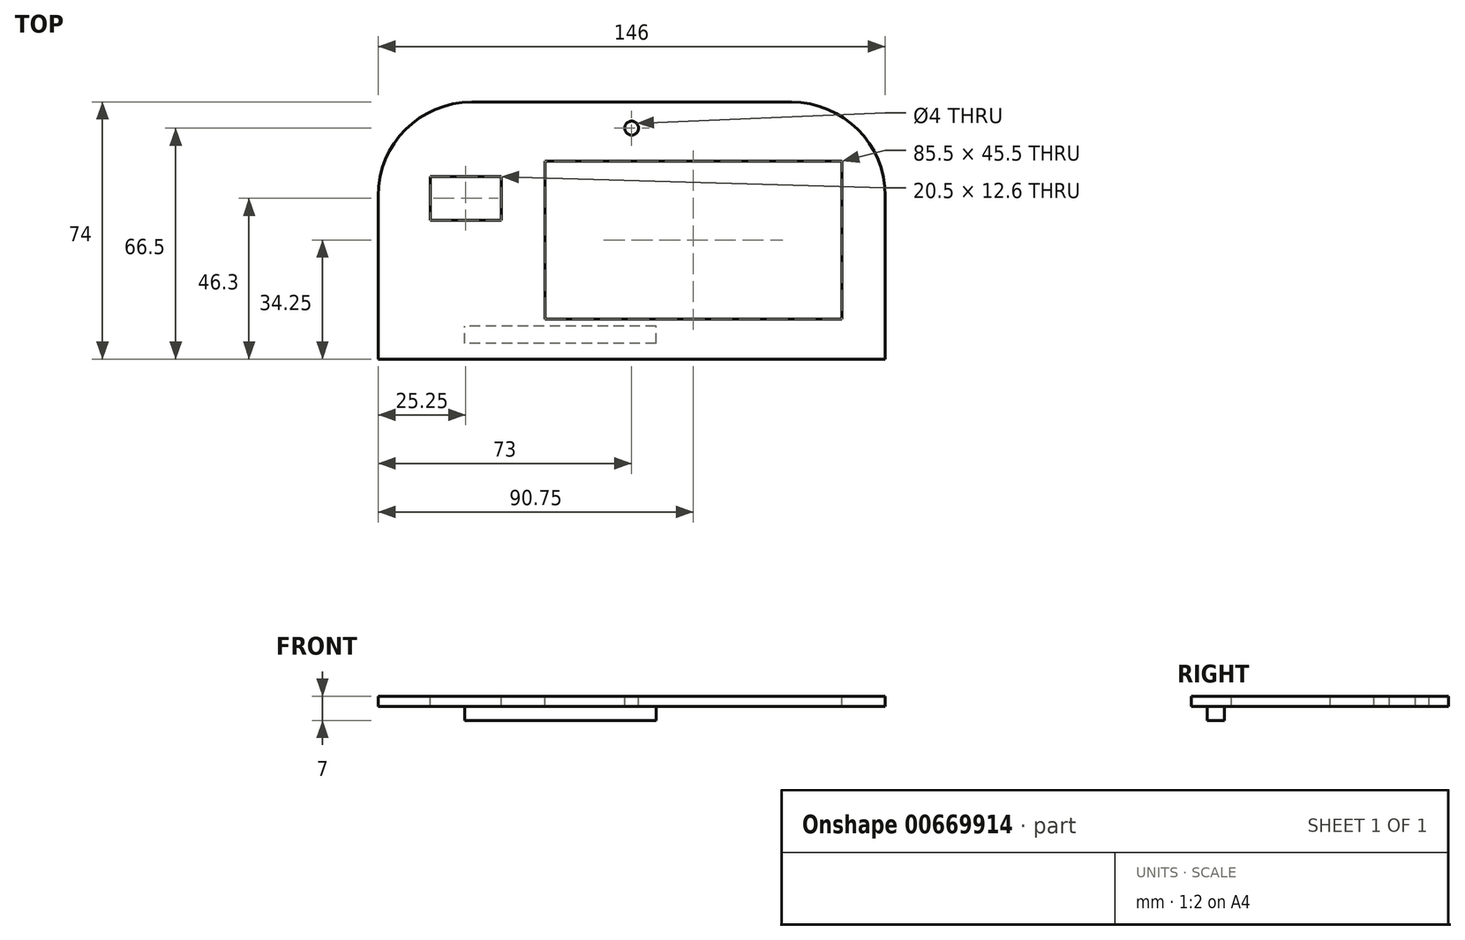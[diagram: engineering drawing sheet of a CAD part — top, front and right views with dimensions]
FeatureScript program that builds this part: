
annotation { "Feature Type Name" : "Feature", "Feature Type Description" : "" }
export const myFeature = defineFeature(function(context is Context, id is Id, definition is map)
    precondition{}
    {
        {
            var Q0;
            Q0=qCreatedBy(makeId("Top.planeOp"),FACE);
            var sketch = newSketch(context, id + "F0", { "sketchPlane" : qUnion([Q0])});
            skLineSegment(sketch, "E0.bottom", {"start": v(2.5, 0) * mm, "end": v(143.5, 0) * mm});
            skLineSegment(sketch, "E0.top", {"start": v(27, 74) * mm, "end": v(119, 74) * mm});
            skLineSegment(sketch, "E0.left", {"start": v(0, 4.25) * mm, "end": v(0, 47) * mm});
            skLineSegment(sketch, "E0.right", {"start": v(146, 4.25) * mm, "end": v(146, 47) * mm});
            skArc(sketch, "E1", {"start": v(0, 47) * mm, "mid": v(7.9, 66.1) * mm, "end": v(27, 74) * mm});
            skArc(sketch, "E2", {"start": v(119, 74) * mm, "mid": v(138.1, 66.1) * mm, "end": v(146, 47) * mm});
            skPoint(sketch, "E3.orphan", {"position": v(0, 0) * mm});
            skPoint(sketch, "E4.orphan", {"position": v(146, 0) * mm});
            skLineSegment(sketch, "E5", {"start": v(143.5, 0) * mm, "end": v(146, 0) * mm});
            skLineSegment(sketch, "E6", {"start": v(0, 4.25) * mm, "end": v(0, 0) * mm});
            skLineSegment(sketch, "E7", {"start": v(146, 4.25) * mm, "end": v(146, 0) * mm});
            skLineSegment(sketch, "E8", {"start": v(0, 0) * mm, "end": v(2.5, 0) * mm});
            skSolve(sketch);
        }
        {
            var Q0;
            Q0 = qSketchRegion(id + "F0", true);
            extrude(context, id + "F1", {"entities" : qUnion([Q0]), "depth" : 3 * mm, "offsetDistance" : 25 * mm});
        }
        {
            var Q0;
            Q0=makeQuery(id+"F1.opExtrude","CAP_FACE",FACE,{"disambiguationData":[OSD([sQuery(id+"F0.wireOp",EDGE,"E0.bottom"),sQuery(id+"F0.wireOp",EDGE,"E0.top"),sQuery(id+"F0.wireOp",EDGE,"E0.left"),sQuery(id+"F0.wireOp",EDGE,"E0.right"),sQuery(id+"F0.wireOp",EDGE,"E1"),sQuery(id+"F0.wireOp",EDGE,"E2"),sQuery(id+"F0.wireOp",EDGE,"dhhxstFw-3Tst-NUUc-EK1n-M0zJhvrsD8Aj.top"),sQuery(id+"F0.wireOp",EDGE,"dhhxstFw-3Tst-NUUc-EK1n-M0zJhvrsD8Aj.left"),sQuery(id+"F0.wireOp",EDGE,"dhhxstFw-3Tst-NUUc-EK1n-M0zJhvrsD8Aj.right"),sQuery(id+"F0.wireOp",EDGE,"TwRv269z-837p-riKi-pISE-XhmJoBw1bLQM"),sQuery(id+"F0.wireOp",EDGE,"1nHeJ8zB-0Bzm-IVgi-laBw-rmo1qJihY1fU"),sQuery(id+"F0.wireOp",EDGE,"EFsbCau8-Kk7Z-T8ND-cFak-pafifdm0BLnr"),sQuery(id+"F0.wireOp",EDGE,"QrewOOia-0hZ0-GSZ7-8uZE-veFKSXKjfm9m"),sQuery(id+"F0.wireOp",EDGE,"qgbczoHn-gC8x-VHlO-2qKL-WriCtDE82gYO"),sQuery(id+"F0.wireOp",EDGE,"J7cCSEcf-Dw3S-IY75-znc3-abka4nDOP1Rm.bottom"),sQuery(id+"F0.wireOp",EDGE,"2mJ6ZCcF-EUu8-ouHu-8j3f-lcy0OV2RSlLl"),sQuery(id+"F0.wireOp",EDGE,"4P5ibF8n-WJ9x-f0f6-TafT-uwGbCgyimzqx"),sQuery(id+"F0.wireOp",EDGE,"El9AkxiO-B9XT-utHc-faxD-VJNF58IxuTyR")])],"isStart":false});
            var sketch = newSketch(context, id + "F2", { "sketchPlane" : qUnion([Q0])});
            skLineSegment(sketch, "E9.bottom", {"start": v(15, 52.6) * mm, "end": v(35.5, 52.6) * mm});
            skLineSegment(sketch, "E9.top", {"start": v(15, 40) * mm, "end": v(35.5, 40) * mm});
            skLineSegment(sketch, "E9.left", {"start": v(15, 52.6) * mm, "end": v(15, 40) * mm});
            skLineSegment(sketch, "E9.right", {"start": v(35.5, 52.6) * mm, "end": v(35.5, 40) * mm});
            skLineSegment(sketch, "E10", {"start": v(65.5, 74) * mm, "end": v(65.5, 59) * mm, "construction": true});
            skLineSegment(sketch, "E11", {"start": v(65.5, 59) * mm, "end": v(80.5, 59) * mm, "construction": true});
            skLineSegment(sketch, "E12", {"start": v(80.5, 59) * mm, "end": v(80.5, 74) * mm, "construction": true});
            skLineSegment(sketch, "E13", {"start": v(73, 74) * mm, "end": v(73, 54.88) * mm, "construction": true});
            skLineSegment(sketch, "E14", {"start": v(65.5, 66.5) * mm, "end": v(80.5, 66.5) * mm, "construction": true});
            skCircle(sketch, "E15", {"center": v(73, 66.5) * mm, "radius": 2 * mm});
            skLineSegment(sketch, "E16.bottom", {"start": v(48, 57) * mm, "end": v(133.5, 57) * mm});
            skLineSegment(sketch, "E16.top", {"start": v(48, 11.5) * mm, "end": v(133.5, 11.5) * mm});
            skLineSegment(sketch, "E16.left", {"start": v(48, 57) * mm, "end": v(48, 11.5) * mm});
            skLineSegment(sketch, "E16.right", {"start": v(133.5, 57) * mm, "end": v(133.5, 11.5) * mm});
            skSolve(sketch);
        }
        {
            var Q0;
            Q0 = qSketchRegion(id + "F2", true);
            extrude(context, id + "F3", {"entities" : qUnion([Q0]), "operationType" : NewBodyOperationType.REMOVE, "oppositeDirection" : true, "depth" : 3 * mm, "offsetDistance" : 25 * mm});
        }
        {
            var Q0;
            Q0=makeQuery(id+"F1.opExtrude","CAP_FACE",FACE,{"disambiguationData":[OSD([sQuery(id+"F0.wireOp",EDGE,"E0.bottom"),sQuery(id+"F0.wireOp",EDGE,"E0.top"),sQuery(id+"F0.wireOp",EDGE,"E0.left"),sQuery(id+"F0.wireOp",EDGE,"E0.right"),sQuery(id+"F0.wireOp",EDGE,"E1"),sQuery(id+"F0.wireOp",EDGE,"E2"),sQuery(id+"F0.wireOp",EDGE,"E5"),sQuery(id+"F0.wireOp",EDGE,"E6"),sQuery(id+"F0.wireOp",EDGE,"E7"),sQuery(id+"F0.wireOp",EDGE,"E8")])],"isStart":true});
            var sketch = newSketch(context, id + "F4", { "sketchPlane" : qUnion([Q0])});
            skLineSegment(sketch, "E17.bottom", {"start": v(80, -4.5) * mm, "end": v(25, -4.5) * mm});
            skLineSegment(sketch, "E17.top", {"start": v(80, -9.5) * mm, "end": v(25, -9.5) * mm});
            skLineSegment(sketch, "E17.left", {"start": v(80, -4.5) * mm, "end": v(80, -9.5) * mm});
            skLineSegment(sketch, "E17.right", {"start": v(25, -4.5) * mm, "end": v(25, -9.5) * mm});
            skSolve(sketch);
        }
        {
            var Q0;
            Q0=makeQuery(id+"F4.imprint","IMPRINT",FACE,{"disambiguationData":[TD([[makeQuery(id+"F4.imprint","IMPRINT",EDGE,{"derivedFrom":sQuery(id+"F4.wireOp",EDGE,"E17.bottom")}),1.0]])]});
            extrude(context, id + "F5", {"entities" : qUnion([Q0]), "operationType" : NewBodyOperationType.ADD, "depth" : 4 * mm, "offsetDistance" : 25 * mm});
        }
    });
